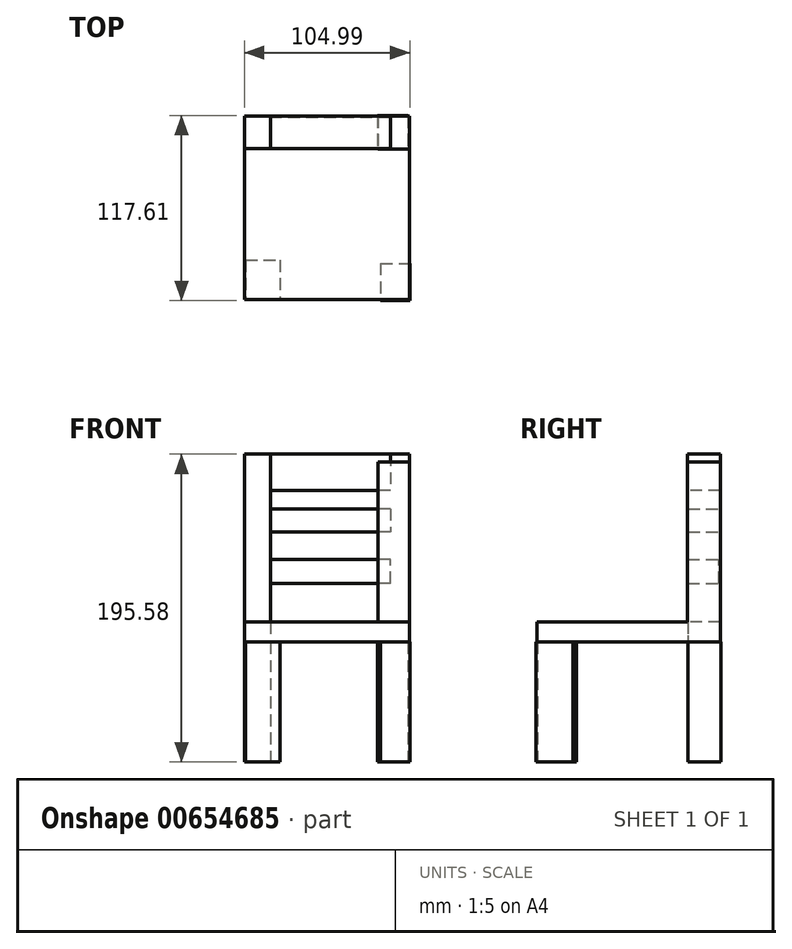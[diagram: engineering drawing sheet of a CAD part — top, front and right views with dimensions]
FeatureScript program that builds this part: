
annotation { "Feature Type Name" : "Feature", "Feature Type Description" : "" }
export const myFeature = defineFeature(function(context is Context, id is Id, definition is map)
    precondition{}
    {
        {
            var Q0;
            Q0=qCreatedBy(makeId("Top.planeOp"),FACE);
            var sketch = newSketch(context, id + "F0", { "sketchPlane" : qUnion([Q0])});
            skLineSegment(sketch, "E0.bottom", {"start": v(-57.5, 61.67) * mm, "end": v(-41.07, 61.67) * mm});
            skLineSegment(sketch, "E0.top", {"start": v(-57.5, 41.2) * mm, "end": v(-41.07, 41.2) * mm});
            skLineSegment(sketch, "E0.left", {"start": v(-57.5, 61.67) * mm, "end": v(-57.5, 41.2) * mm});
            skLineSegment(sketch, "E0.right", {"start": v(-41.07, 61.67) * mm, "end": v(-41.07, 41.2) * mm});
            skSolve(sketch);
        }
        {
            var Q0;
            Q0=makeQuery(id+"F0.imprint","IMPRINT",FACE,{"disambiguationData":[TD([[makeQuery(id+"F0.imprint","IMPRINT",EDGE,{"derivedFrom":sQuery(id+"F0.wireOp",EDGE,"E0.bottom")}),-1.0]])]});
            extrude(context, id + "F1", {"entities" : qUnion([Q0]), "depth" : 76.2 * mm, "offsetDistance" : 25.4 * mm});
        }
        {
            var Q0;
            Q0=qCreatedBy(makeId("Top.planeOp"),FACE);
            var sketch = newSketch(context, id + "F2", { "sketchPlane" : qUnion([Q0])});
            skLineSegment(sketch, "E1.bottom", {"start": v(27.1, 62.12) * mm, "end": v(46.5, 62.12) * mm});
            skLineSegment(sketch, "E1.top", {"start": v(27.1, 41.08) * mm, "end": v(46.5, 41.08) * mm});
            skLineSegment(sketch, "E1.left", {"start": v(27.1, 62.12) * mm, "end": v(27.1, 41.08) * mm});
            skLineSegment(sketch, "E1.right", {"start": v(46.5, 62.12) * mm, "end": v(46.5, 41.08) * mm});
            skSolve(sketch);
        }
        {
            var Q0;
            Q0=makeQuery(id+"F2.imprint","IMPRINT",FACE,{"disambiguationData":[TD([[makeQuery(id+"F2.imprint","IMPRINT",EDGE,{"derivedFrom":sQuery(id+"F2.wireOp",EDGE,"E1.bottom")}),-1.0]])]});
            extrude(context, id + "F3", {"entities" : qUnion([Q0]), "depth" : 76.2 * mm, "offsetDistance" : 25.4 * mm});
        }
        {
            var Q0;
            Q0=qCreatedBy(makeId("Top.planeOp"),FACE);
            var sketch = newSketch(context, id + "F4", { "sketchPlane" : qUnion([Q0])});
            skLineSegment(sketch, "E2.bottom", {"start": v(-56.84, -29.73) * mm, "end": v(-35, -29.73) * mm});
            skLineSegment(sketch, "E2.top", {"start": v(-56.84, -54.27) * mm, "end": v(-35, -54.27) * mm});
            skLineSegment(sketch, "E2.left", {"start": v(-56.84, -29.73) * mm, "end": v(-56.84, -54.27) * mm});
            skLineSegment(sketch, "E2.right", {"start": v(-35, -29.73) * mm, "end": v(-35, -54.27) * mm});
            skSolve(sketch);
        }
        {
            var Q0;
            Q0=makeQuery(id+"F4.imprint","IMPRINT",FACE,{"disambiguationData":[TD([[makeQuery(id+"F4.imprint","IMPRINT",EDGE,{"derivedFrom":sQuery(id+"F4.wireOp",EDGE,"E2.bottom")}),-1.0]])]});
            extrude(context, id + "F5", {"entities" : qUnion([Q0]), "depth" : 76.2 * mm, "offsetDistance" : 25.4 * mm});
        }
        {
            var Q0;
            Q0=qCreatedBy(makeId("Top.planeOp"),FACE);
            var sketch = newSketch(context, id + "F6", { "sketchPlane" : qUnion([Q0])});
            skLineSegment(sketch, "E3.bottom", {"start": v(29.03, -31.88) * mm, "end": v(47.49, -31.88) * mm});
            skLineSegment(sketch, "E3.top", {"start": v(29.03, -55.5) * mm, "end": v(47.49, -55.5) * mm});
            skLineSegment(sketch, "E3.left", {"start": v(29.03, -31.88) * mm, "end": v(29.03, -55.5) * mm});
            skLineSegment(sketch, "E3.right", {"start": v(47.49, -31.88) * mm, "end": v(47.49, -55.5) * mm});
            skSolve(sketch);
        }
        {
            var Q0;
            Q0=makeQuery(id+"F6.imprint","IMPRINT",FACE,{"disambiguationData":[TD([[makeQuery(id+"F6.imprint","IMPRINT",EDGE,{"derivedFrom":sQuery(id+"F6.wireOp",EDGE,"E3.bottom")}),-1.0]])]});
            extrude(context, id + "F7", {"entities" : qUnion([Q0]), "depth" : 76.2 * mm, "offsetDistance" : 25.4 * mm});
        }
        {
            var Q0;
            Q0=makeQuery(id+"F1.opExtrude","CAP_FACE",FACE,{"disambiguationData":[OSD([sQuery(id+"F0.wireOp",EDGE,"E0.bottom"),sQuery(id+"F0.wireOp",EDGE,"E0.top"),sQuery(id+"F0.wireOp",EDGE,"E0.left"),sQuery(id+"F0.wireOp",EDGE,"E0.right")])],"isStart":false});
            var sketch = newSketch(context, id + "F8", { "sketchPlane" : qUnion([Q0])});
            skLineSegment(sketch, "E4.bottom", {"start": v(-57.5, 61.67) * mm, "end": v(47.15, 61.67) * mm});
            skLineSegment(sketch, "E4.top", {"start": v(-57.5, -54.75) * mm, "end": v(47.15, -54.75) * mm});
            skLineSegment(sketch, "E4.left", {"start": v(-57.5, 61.67) * mm, "end": v(-57.5, -54.75) * mm});
            skLineSegment(sketch, "E4.right", {"start": v(47.15, 61.67) * mm, "end": v(47.15, -54.75) * mm});
            skSolve(sketch);
        }
        {
            var Q0;
            {var subQ2=sQuery(id+"F8.wireOp",EDGE,"E4.top");Q0=makeQuery(id+"F8.imprint","IMPRINT",FACE,{"disambiguationData":[TD([[makeQuery(id+"F8.imprint","IMPRINT",EDGE,{"derivedFrom":subQ2}),1.0]])]});}
            extrude(context, id + "F9", {"entities" : qUnion([Q0]), "depth" : 12.7 * mm, "offsetDistance" : 25.4 * mm});
        }
        {
            var Q0;
            Q0=makeQuery(id+"F1.opExtrude","CAP_FACE",FACE,{"disambiguationData":[OSD([sQuery(id+"F0.wireOp",EDGE,"E0.bottom"),sQuery(id+"F0.wireOp",EDGE,"E0.top"),sQuery(id+"F0.wireOp",EDGE,"E0.left"),sQuery(id+"F0.wireOp",EDGE,"E0.right")])],"isStart":false});
            var sketch = newSketch(context, id + "F10", { "sketchPlane" : qUnion([Q0])});
            skSolve(sketch);
        }
        {
            var Q0;
            Q0=makeQuery(id+"F10.imprint","IMPRINT",FACE,{"disambiguationData":[TD([[makeQuery(id+"F10.imprint","IMPRINT",EDGE,{"derivedFrom":makeQuery(id+"F1.opExtrude","CAP_EDGE",EDGE,{"disambiguationData":[OSD([sQuery(id+"F0.wireOp",EDGE,"E0.bottom")])],"isStart":false})}),-1.0]])]});
            extrude(context, id + "F11", {"entities" : qUnion([Q0]), "depth" : 101.6 * mm, "offsetDistance" : 25.4 * mm});
        }
        {
            var Q0;
            Q0=makeQuery(id+"F9.opExtrude","CAP_FACE",FACE,{"disambiguationData":[OSD([sQuery(id+"F0.wireOp",EDGE,"E0.top"),sQuery(id+"F0.wireOp",EDGE,"E0.right"),sQuery(id+"F8.wireOp",EDGE,"E4.bottom"),sQuery(id+"F8.wireOp",EDGE,"E4.top"),sQuery(id+"F8.wireOp",EDGE,"E4.left"),sQuery(id+"F8.wireOp",EDGE,"E4.right")])],"isStart":false});
            var sketch = newSketch(context, id + "F12", { "sketchPlane" : qUnion([Q0])});
            skLineSegment(sketch, "E5.bottom", {"start": v(47.15, 61.67) * mm, "end": v(27.37, 61.67) * mm});
            skLineSegment(sketch, "E5.top", {"start": v(47.15, 40.76) * mm, "end": v(27.37, 40.76) * mm});
            skLineSegment(sketch, "E5.left", {"start": v(47.15, 61.67) * mm, "end": v(47.15, 40.76) * mm});
            skLineSegment(sketch, "E5.right", {"start": v(27.37, 61.67) * mm, "end": v(27.37, 40.76) * mm});
            skSolve(sketch);
        }
        {
            var Q0;
            Q0=makeQuery(id+"F12.imprint","IMPRINT",FACE,{"disambiguationData":[TD([[makeQuery(id+"F12.imprint","IMPRINT",EDGE,{"derivedFrom":sQuery(id+"F12.wireOp",EDGE,"E5.bottom")}),-1.0]])]});
            extrude(context, id + "F13", {"entities" : qUnion([Q0]), "operationType" : NewBodyOperationType.ADD, "depth" : 101.6 * mm, "offsetDistance" : 25.4 * mm});
        }
        {
            var Q0;
            Q0=makeQuery(id+"F11.opExtrude","CAP_FACE",FACE,{"disambiguationData":[OSD([sQuery(id+"F0.wireOp",EDGE,"E0.bottom"),sQuery(id+"F0.wireOp",EDGE,"E0.top"),sQuery(id+"F0.wireOp",EDGE,"E0.left"),sQuery(id+"F0.wireOp",EDGE,"E0.right")])],"isStart":false});
            var sketch = newSketch(context, id + "F14", { "sketchPlane" : qUnion([Q0])});
            skLineSegment(sketch, "E6.bottom", {"start": v(-57.5, 61.67) * mm, "end": v(-41.07, 61.67) * mm});
            skLineSegment(sketch, "E6.top", {"start": v(-57.5, 41.2) * mm, "end": v(-41.07, 41.2) * mm});
            skLineSegment(sketch, "E6.left", {"start": v(-57.5, 61.67) * mm, "end": v(-57.5, 41.2) * mm});
            skLineSegment(sketch, "E6.right", {"start": v(-41.07, 61.67) * mm, "end": v(-41.07, 41.2) * mm});
            skSolve(sketch);
        }
        {
            var Q0;
            Q0=makeQuery(id+"F14.imprint","IMPRINT",FACE,{"disambiguationData":[TD([[makeQuery(id+"F14.imprint","IMPRINT",EDGE,{"derivedFrom":sQuery(id+"F14.wireOp",EDGE,"E6.bottom")}),-1.0]])]});
            extrude(context, id + "F15", {"entities" : qUnion([Q0]), "operationType" : NewBodyOperationType.ADD, "depth" : 17.78 * mm, "offsetDistance" : 25.4 * mm});
        }
        {
            var Q0;
            Q0=makeQuery(id+"F15.boolean.opBoolean","MERGE",FACE,{"derivedFrom":[makeQuery(id+"F11.opExtrude","SWEPT_FACE",FACE,{"disambiguationData":[OSD([sQuery(id+"F0.wireOp",EDGE,"E0.right")])]}),makeQuery(id+"F15.opExtrude","SWEPT_FACE",FACE,{"disambiguationData":[OSD([sQuery(id+"F14.wireOp",EDGE,"E6.right")])]})]});
            var sketch = newSketch(context, id + "F16", { "sketchPlane" : qUnion([Q0])});
            skLineSegment(sketch, "E7.bottom", {"start": v(61.67, 195.58) * mm, "end": v(41.2, 195.58) * mm});
            skLineSegment(sketch, "E7.top", {"start": v(61.67, 172.42) * mm, "end": v(41.2, 172.42) * mm});
            skLineSegment(sketch, "E7.left", {"start": v(61.67, 195.58) * mm, "end": v(61.67, 172.42) * mm});
            skLineSegment(sketch, "E7.right", {"start": v(41.2, 195.58) * mm, "end": v(41.2, 172.42) * mm});
            skSolve(sketch);
        }
        {
            var Q0;
            {var subQ0=sQuery(id+"F16.wireOp",EDGE,"E7.top");Q0=makeQuery(id+"F16.imprint","IMPRINT",FACE,{"disambiguationData":[TD([[makeQuery(id+"F16.imprint","IMPRINT",EDGE,{"derivedFrom":subQ0}),1.0]])]});}
            var sketch = newSketch(context, id + "F17", { "sketchPlane" : qUnion([Q0])});
            skLineSegment(sketch, "E8.bottom", {"start": v(41.06, 113.48) * mm, "end": v(60.79, 113.48) * mm});
            skLineSegment(sketch, "E8.top", {"start": v(41.06, 128.59) * mm, "end": v(60.79, 128.59) * mm});
            skLineSegment(sketch, "E8.left", {"start": v(41.06, 113.48) * mm, "end": v(41.06, 128.59) * mm});
            skLineSegment(sketch, "E8.right", {"start": v(60.79, 113.48) * mm, "end": v(60.79, 128.59) * mm});
            skSolve(sketch);
        }
        {
            var Q0;
            Q0=makeQuery(id+"F17.imprint","IMPRINT",FACE,{"disambiguationData":[TD([[makeQuery(id+"F17.imprint","IMPRINT",EDGE,{"derivedFrom":sQuery(id+"F17.wireOp",EDGE,"E8.bottom")}),1.0]])]});
            extrude(context, id + "F18", {"entities" : qUnion([Q0]), "depth" : 76.2 * mm, "offsetDistance" : 25.4 * mm});
        }
        {
            var Q0;
            Q0=makeQuery(id+"F16.imprint","IMPRINT",FACE,{"disambiguationData":[TD([[makeQuery(id+"F16.imprint","IMPRINT",EDGE,{"derivedFrom":sQuery(id+"F16.wireOp",EDGE,"E7.bottom")}),1.0]])]});
            extrude(context, id + "F19", {"entities" : qUnion([Q0]), "depth" : 76.2 * mm, "offsetDistance" : 25.4 * mm});
        }
        {
            var Q0;
            Q0=makeQuery(id+"F13.opExtrude","CAP_FACE",FACE,{"disambiguationData":[OSD([sQuery(id+"F12.wireOp",EDGE,"E5.bottom"),sQuery(id+"F12.wireOp",EDGE,"E5.top"),sQuery(id+"F12.wireOp",EDGE,"E5.left"),sQuery(id+"F12.wireOp",EDGE,"E5.right")])],"isStart":false});
            var sketch = newSketch(context, id + "F20", { "sketchPlane" : qUnion([Q0])});
            skLineSegment(sketch, "E9.bottom", {"start": v(47.15, 61.67) * mm, "end": v(35.1, 61.67) * mm});
            skLineSegment(sketch, "E9.top", {"start": v(47.15, 40.76) * mm, "end": v(35.1, 40.76) * mm});
            skLineSegment(sketch, "E9.left", {"start": v(47.15, 61.67) * mm, "end": v(47.15, 40.76) * mm});
            skLineSegment(sketch, "E9.right", {"start": v(35.1, 61.67) * mm, "end": v(35.1, 40.76) * mm});
            skSolve(sketch);
        }
        {
            var Q0;
            Q0=makeQuery(id+"F20.imprint","IMPRINT",FACE,{"disambiguationData":[TD([[makeQuery(id+"F20.imprint","IMPRINT",EDGE,{"derivedFrom":sQuery(id+"F20.wireOp",EDGE,"E9.bottom")}),-1.0]])]});
            extrude(context, id + "F21", {"entities" : qUnion([Q0]), "depth" : 5.08 * mm, "offsetDistance" : 25.4 * mm});
        }
        {
            var Q0;
            Q0=makeQuery(id+"F15.boolean.opBoolean","MERGE",FACE,{"derivedFrom":[makeQuery(id+"F11.opExtrude","SWEPT_FACE",FACE,{"disambiguationData":[OSD([sQuery(id+"F0.wireOp",EDGE,"E0.right")])]}),makeQuery(id+"F15.opExtrude","SWEPT_FACE",FACE,{"disambiguationData":[OSD([sQuery(id+"F14.wireOp",EDGE,"E6.right")])]})]});
            var sketch = newSketch(context, id + "F22", { "sketchPlane" : qUnion([Q0])});
            skLineSegment(sketch, "E10.bottom", {"start": v(41.2, 160.9) * mm, "end": v(61.67, 160.9) * mm});
            skLineSegment(sketch, "E10.top", {"start": v(41.2, 146.16) * mm, "end": v(61.67, 146.16) * mm});
            skLineSegment(sketch, "E10.left", {"start": v(41.2, 160.9) * mm, "end": v(41.2, 146.16) * mm});
            skLineSegment(sketch, "E10.right", {"start": v(61.67, 160.9) * mm, "end": v(61.67, 146.16) * mm});
            skSolve(sketch);
        }
        {
            var Q0;
            Q0=makeQuery(id+"F22.imprint","IMPRINT",FACE,{"disambiguationData":[TD([[makeQuery(id+"F22.imprint","IMPRINT",EDGE,{"derivedFrom":sQuery(id+"F22.wireOp",EDGE,"E10.bottom")}),-1.0]])]});
            extrude(context, id + "F23", {"entities" : qUnion([Q0]), "depth" : 76.2 * mm, "offsetDistance" : 25.4 * mm});
        }
    });
